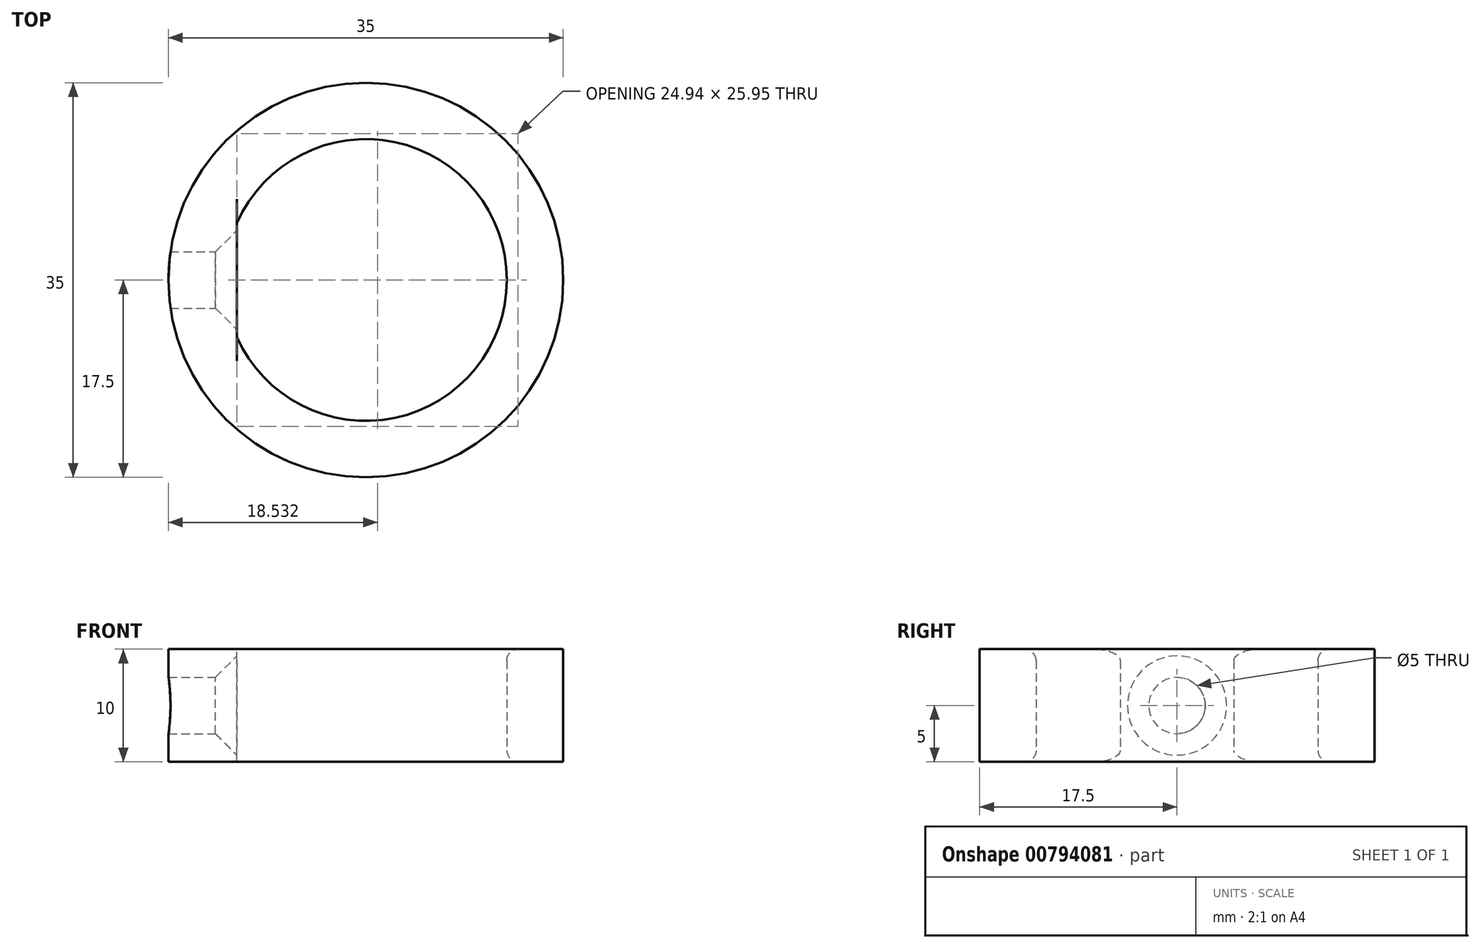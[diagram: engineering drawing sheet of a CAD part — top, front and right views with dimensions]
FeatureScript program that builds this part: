
annotation { "Feature Type Name" : "Feature", "Feature Type Description" : "" }
export const myFeature = defineFeature(function(context is Context, id is Id, definition is map)
    precondition{}
    {
        {
            var Q0;
            Q0=qCreatedBy(makeId("Top.planeOp"),FACE);
            var sketch = newSketch(context, id + "F0", { "sketchPlane" : qUnion([Q0])});
            skCircle(sketch, "E0", {"center": v(0, 0) * mm, "radius": 17.5 * mm});
            skCircle(sketch, "E1", {"center": v(0, 0) * mm, "radius": 12.5 * mm});
            skPoint(sketch, "E2", {"position": v(-17.5, 0) * mm});
            skLineSegment(sketch, "E3", {"start": v(-11.44, 5.05) * mm, "end": v(-11.44, -5.05) * mm});
            skSolve(sketch);
        }
        {
            var Q0;
            Q0=makeQuery(id+"F0.imprint","IMPRINT",FACE,{"disambiguationData":[TD([[makeQuery(id+"F0.imprint","IMPRINT",EDGE,{"derivedFrom":sQuery(id+"F0.wireOp",EDGE,"E1")}),-1.0]])]});
            extrude(context, id + "F1", {"entities" : qUnion([Q0]), "depth" : 10 * mm, "offsetDistance" : 25 * mm});
        }
        {
            var Q0;
            {var subQ0=sQuery(id+"F0.wireOp",EDGE,"E3");Q0=makeQuery(id+"F0.imprint","IMPRINT",FACE,{"disambiguationData":[TD([[makeQuery(id+"F0.imprint","IMPRINT",EDGE,{"derivedFrom":subQ0}),-1.0]])]});}
            extrude(context, id + "F2", {"entities" : qUnion([Q0]), "operationType" : NewBodyOperationType.ADD, "depth" : 10 * mm, "offsetDistance" : 25 * mm});
        }
        {
            var Q0;
            Q0=makeQuery(id+"F2.opExtrude","SWEPT_FACE",FACE,{"disambiguationData":[OSD([sQuery(id+"F0.wireOp",EDGE,"E3")])]});
            var sketch = newSketch(context, id + "F3", { "sketchPlane" : qUnion([Q0])});
            skLineSegment(sketch, "E4", {"start": v(-5.05, 0) * mm, "end": v(5.05, 10) * mm});
            skPoint(sketch, "E5", {"position": v(0, 5) * mm});
            skSolve(sketch);
        }
        {
            var Q0;
            Q0=sQuery(id+"F3.wireOp",VERTEX,"E5");
            var Q1;
            Q1=makeQuery(id+"F1.opExtrude","SWEPT_BODY",BODY,{"disambiguationData":[OSD([sQuery(id+"F0.wireOp",EDGE,"E0"),sQuery(id+"F0.wireOp",EDGE,"E1")])]});
            hole(context, id + "F4", {"style" : HoleStyle.C_SINK, "endStyle" : HoleEndStyle.THROUGH, "holeDiameter" : 5 * mm, "cSinkDiameter" : 8.8 * mm, "cSinkAngle" : 90 * degree, "majorDiameter" : 5 * mm, "isTappedThrough" : true, "tappedDepth" : 12 * mm, "tapClearance" : 3, "locations" : qUnion([Q0]), "scope" : qUnion([Q1])});
        }
        {
            var Q0;
            Q0=makeQuery(id+"F1.opExtrude","CAP_EDGE",EDGE,{"disambiguationData":[OSD([sQuery(id+"F0.wireOp",EDGE,"E1")])],"isStart":false});
            fillet(context, id + "F5", {"entities" : qUnion([Q0]), "radius" : 1 * mm, "tangentPropagation" : true, "allowEdgeOverflow" : false});
        }
        {
            var Q0;
            Q0=makeQuery(id+"F1.opExtrude","CAP_EDGE",EDGE,{"disambiguationData":[OSD([sQuery(id+"F0.wireOp",EDGE,"E1")])],"isStart":true});
            fillet(context, id + "F6", {"entities" : qUnion([Q0]), "radius" : 1 * mm, "tangentPropagation" : true, "allowEdgeOverflow" : false});
        }
    });
